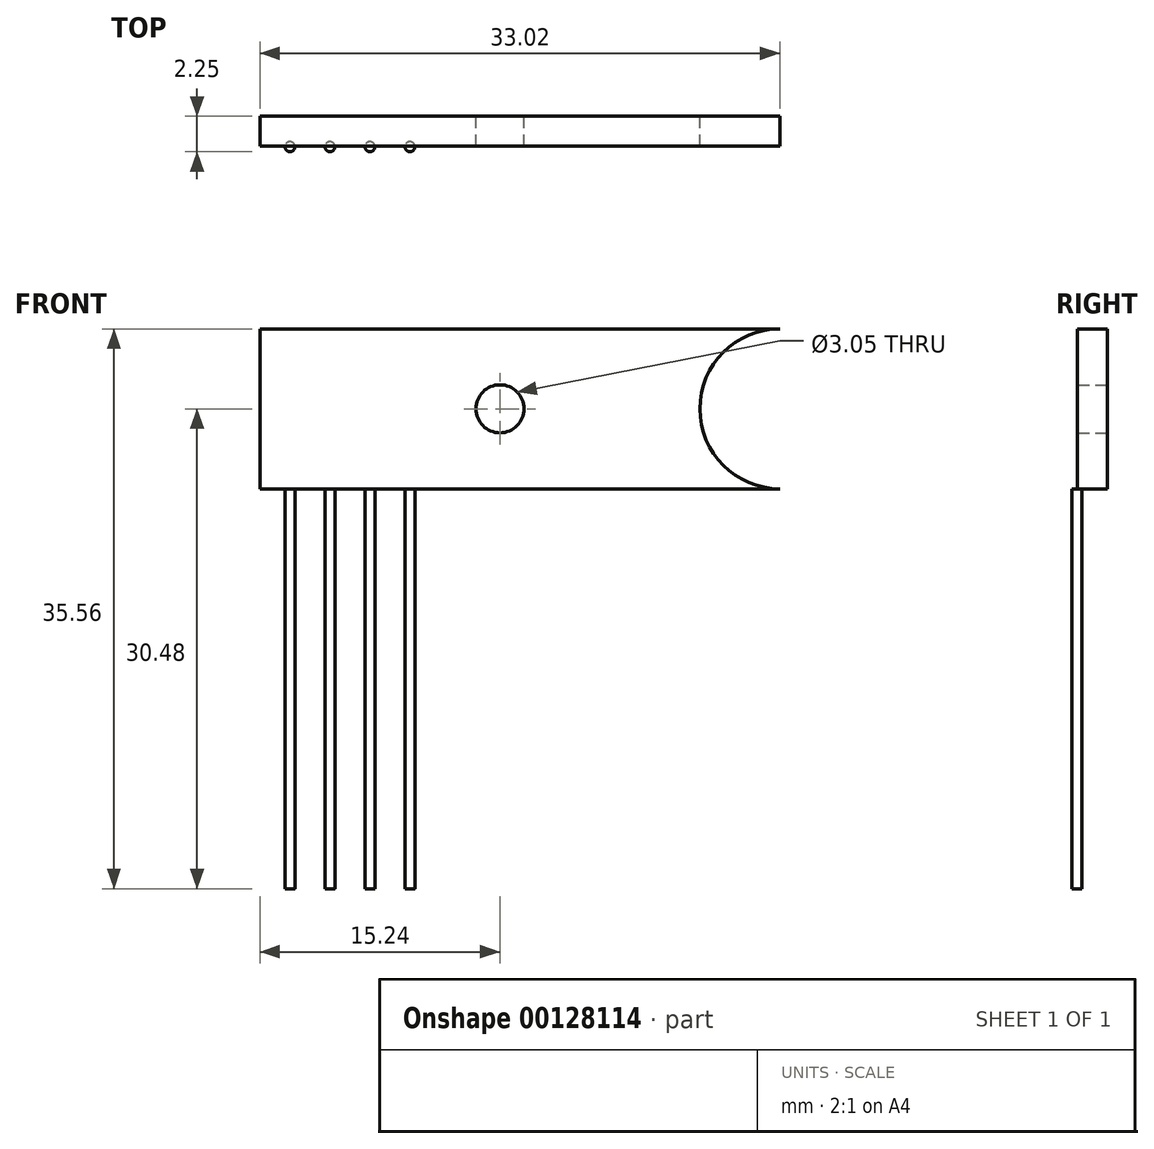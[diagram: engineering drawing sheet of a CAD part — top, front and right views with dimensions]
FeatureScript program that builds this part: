
annotation { "Feature Type Name" : "Feature", "Feature Type Description" : "" }
export const myFeature = defineFeature(function(context is Context, id is Id, definition is map)
    precondition{}
    {
        {
            var Q0;
            Q0=qCreatedBy(makeId("Front.planeOp"),FACE);
            var sketch = newSketch(context, id + "F0", { "sketchPlane" : qUnion([Q0])});
            skCircle(sketch, "E0", {"center": v(0, 0) * mm, "radius": 5.08 * mm});
            skLineSegment(sketch, "E1.bottom", {"start": v(0, 5.08) * mm, "end": v(-33.02, 5.08) * mm});
            skLineSegment(sketch, "E1.top", {"start": v(0, -5.08) * mm, "end": v(-33.02, -5.08) * mm});
            skLineSegment(sketch, "E1.left", {"start": v(0, 5.08) * mm, "end": v(0, -5.08) * mm});
            skLineSegment(sketch, "E1.right", {"start": v(-33.02, 5.08) * mm, "end": v(-33.02, -5.08) * mm});
            skCircle(sketch, "E2", {"center": v(-17.78, 0) * mm, "radius": 1.52 * mm});
            skSolve(sketch);
        }
        {
            var Q0;
            Q0 = qSketchRegion(id + "F0", true);
            extrude(context, id + "F1", {"entities" : qUnion([Q0]), "depth" : 1.9 * mm});
        }
        {
            var Q0;
            Q0=makeQuery(id+"F7tgGqrMzcgcFxs_1.boolean.opBoolean","MERGE",FACE,{"derivedFrom":[makeQuery(id+"F1.opExtrude","SWEPT_FACE",FACE,{"disambiguationData":[OSD([sQuery(id+"F0.wireOp",EDGE,"E1.top")])]}),makeQuery(id+"F7tgGqrMzcgcFxs_1.opExtrude","SWEPT_FACE",FACE,{"disambiguationData":[OSD([sQuery(id+"FLyghF4MLhnBqlZ_1.wireOp",EDGE,"7inABKFF-CtzZ-Bpgl-zZnN-v0r5DOstO2gn")])]}),makeQuery(id+"F7tgGqrMzcgcFxs_1.opExtrude","SWEPT_FACE",FACE,{"disambiguationData":[OSD([sQuery(id+"FLyghF4MLhnBqlZ_1.wireOp",EDGE,"724eed2b-d7b5-41d7-a814-04bd2c85835f.1.0.1")])]}),makeQuery(id+"F7tgGqrMzcgcFxs_1.opExtrude","SWEPT_FACE",FACE,{"disambiguationData":[OSD([sQuery(id+"FLyghF4MLhnBqlZ_1.wireOp",EDGE,"724eed2b-d7b5-41d7-a814-04bd2c85835f.2.0.1")])]}),makeQuery(id+"F7tgGqrMzcgcFxs_1.opExtrude","SWEPT_FACE",FACE,{"disambiguationData":[OSD([sQuery(id+"FLyghF4MLhnBqlZ_1.wireOp",EDGE,"724eed2b-d7b5-41d7-a814-04bd2c85835f.3.0.1")])]})]});
            var sketch = newSketch(context, id + "F2", { "sketchPlane" : qUnion([Q0])});
            skCircle(sketch, "E3", {"center": v(-31.12, 1.93) * mm, "radius": 0.32 * mm});
            skCircle(sketch, "E4", {"center": v(-28.58, 1.93) * mm, "radius": 0.32 * mm});
            skCircle(sketch, "E5", {"center": v(-26.04, 1.93) * mm, "radius": 0.32 * mm});
            skCircle(sketch, "E6", {"center": v(-23.5, 1.93) * mm, "radius": 0.32 * mm});
            skSolve(sketch);
        }
        {
            var Q0;
            Q0 = qSketchRegion(id + "F2", true);
            extrude(context, id + "F3", {"entities" : qUnion([Q0]), "operationType" : NewBodyOperationType.ADD, "depth" : 25.4 * mm});
        }
        {
            var Q0;
            Q0=makeQuery(id+"F1.opExtrude","CAP_FACE",FACE,{"disambiguationData":[OSD([sQuery(id+"F0.wireOp",EDGE,"E0"),sQuery(id+"F0.wireOp",EDGE,"E1.bottom"),sQuery(id+"F0.wireOp",EDGE,"E1.top"),sQuery(id+"F0.wireOp",EDGE,"E1.right"),sQuery(id+"F0.wireOp",EDGE,"E2")])],"isStart":true});
            var sketch = newSketch(context, id + "F4", { "sketchPlane" : qUnion([Q0])});
            skCircle(sketch, "E7", {"center": v(0, 0) * mm, "radius": 5.08 * mm});
            skSolve(sketch);
        }
        {
            var Q0;
            Q0 = qSketchRegion(id + "F4", true);
            extrude(context, id + "F5", {"entities" : qUnion([Q0]), "operationType" : NewBodyOperationType.REMOVE, "oppositeDirection" : true, "depth" : 3.84 * mm});
        }
    });
